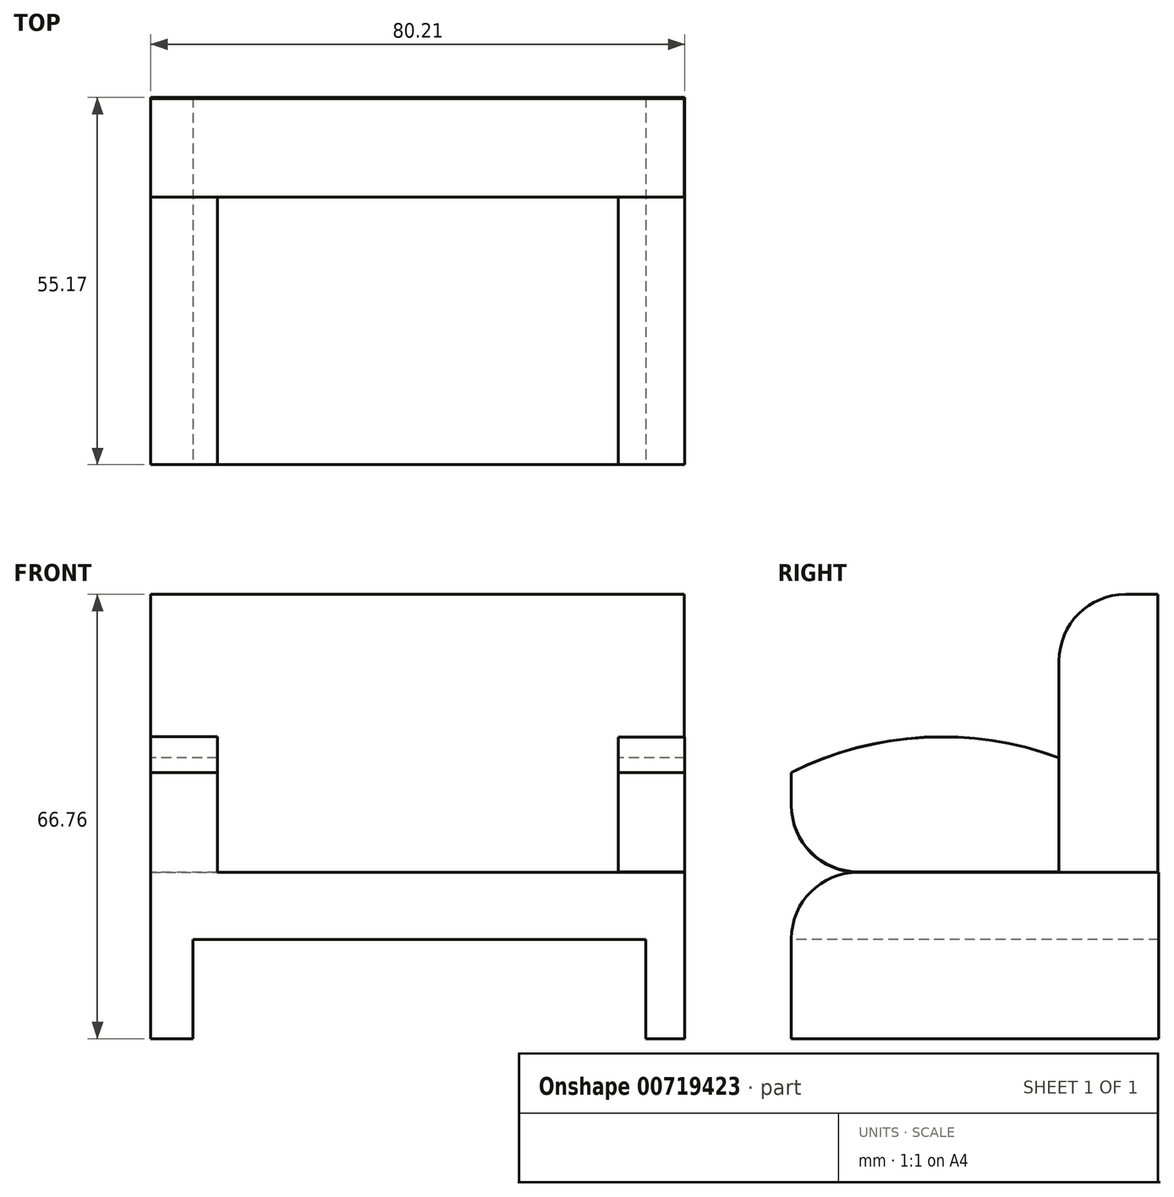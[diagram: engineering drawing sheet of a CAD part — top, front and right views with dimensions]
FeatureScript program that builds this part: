
annotation { "Feature Type Name" : "Feature", "Feature Type Description" : "" }
export const myFeature = defineFeature(function(context is Context, id is Id, definition is map)
    precondition{}
    {
        {
            var Q0;
            Q0=qCreatedBy(makeId("Top.planeOp"),FACE);
            var sketch = newSketch(context, id + "F0", { "sketchPlane" : qUnion([Q0])});
            skLineSegment(sketch, "E0.bottom", {"start": v(0, 0) * mm, "end": v(80.21, 0) * mm});
            skLineSegment(sketch, "E0.top", {"start": v(0, 55.17) * mm, "end": v(80.21, 55.17) * mm});
            skLineSegment(sketch, "E0.left", {"start": v(0, 0) * mm, "end": v(0, 55.17) * mm});
            skLineSegment(sketch, "E0.right", {"start": v(80.21, 0) * mm, "end": v(80.21, 55.17) * mm});
            skSolve(sketch);
        }
        {
            var Q0;
            Q0=makeQuery(id+"F0.imprint","IMPRINT",FACE,{"disambiguationData":[TD([[makeQuery(id+"F0.imprint","IMPRINT",EDGE,{"derivedFrom":sQuery(id+"F0.wireOp",EDGE,"E0.bottom")}),1.0]])]});
            extrude(context, id + "F1", {"entities" : qUnion([Q0]), "depth" : 25 * mm, "offsetDistance" : 25 * mm});
        }
        {
            var Q0;
            Q0=qCreatedBy(makeId("Front.planeOp"),FACE);
            cPlane(context, id + "F2", {"entities" : qUnion([Q0]), "cplaneType" : CPlaneType.OFFSET, "offset" : 55 * mm, "oppositeDirection" : true, "width" : 150 * mm, "height" : 150 * mm});
        }
        {
            var Q0;
            Q0=qCreatedBy(id+"F2.planeOp",FACE);
            var sketch = newSketch(context, id + "F3", { "sketchPlane" : qUnion([Q0])});
            skLineSegment(sketch, "E1.bottom", {"start": v(80.1, 0) * mm, "end": v(0, 0) * mm});
            skLineSegment(sketch, "E1.top", {"start": v(80.1, 66.76) * mm, "end": v(0, 66.76) * mm});
            skLineSegment(sketch, "E1.left", {"start": v(80.1, 0) * mm, "end": v(80.1, 66.76) * mm});
            skLineSegment(sketch, "E1.right", {"start": v(0, 0) * mm, "end": v(0, 66.76) * mm});
            skSolve(sketch);
        }
        {
            var Q0;
            Q0=qSketchRegion(id+"F3",true);
            extrude(context, id + "F4", {"entities" : qUnion([Q0]), "operationType" : NewBodyOperationType.ADD, "depth" : 14.8 * mm, "offsetDistance" : 25 * mm});
        }
        {
            var Q0;
            Q0=qCreatedBy(makeId("Right.planeOp"),FACE);
            var sketch = newSketch(context, id + "F5", { "sketchPlane" : qUnion([Q0])});
            skArc(sketch, "E2", {"start": v(40.2, 42.2) * mm, "mid": v(19.87, 45.28) * mm, "end": v(0, 40) * mm});
            skLineSegment(sketch, "E3", {"start": v(40.2, 42.2) * mm, "end": v(40.2, 25) * mm});
            skLineSegment(sketch, "E4", {"start": v(40.2, 25) * mm, "end": v(0, 25) * mm});
            skLineSegment(sketch, "E5", {"start": v(0, 25) * mm, "end": v(0, 40) * mm});
            skSolve(sketch);
        }
        {
            var Q0;
            Q0=qSketchRegion(id+"F5",true);
            extrude(context, id + "F6", {"entities" : qUnion([Q0]), "depth" : 10 * mm, "offsetDistance" : 25 * mm});
        }
        {
            var Q0;
            Q0=qCreatedBy(makeId("Right.planeOp"),FACE);
            cPlane(context, id + "F7", {"entities" : qUnion([Q0]), "cplaneType" : CPlaneType.OFFSET, "offset" : 70.21 * mm, "width" : 150 * mm, "height" : 150 * mm});
        }
        {
            var Q0;
            Q0=qCreatedBy(id+"F7.planeOp",FACE);
            var sketch = newSketch(context, id + "F8", { "sketchPlane" : qUnion([Q0])});
            skArc(sketch, "E6", {"start": v(40.2, 42.2) * mm, "mid": v(19.87, 45.27) * mm, "end": v(0, 40) * mm});
            skLineSegment(sketch, "E7", {"start": v(0, 40) * mm, "end": v(0, 25.08) * mm});
            skLineSegment(sketch, "E8", {"start": v(0, 25.08) * mm, "end": v(40.2, 25.08) * mm});
            skLineSegment(sketch, "E9", {"start": v(40.2, 25.08) * mm, "end": v(40.2, 42.2) * mm});
            skSolve(sketch);
        }
        {
            var Q0;
            Q0=qSketchRegion(id+"F8",true);
            extrude(context, id + "F9", {"entities" : qUnion([Q0]), "depth" : 10 * mm, "offsetDistance" : 25 * mm});
        }
        {
            var Q0;
            Q0=qCreatedBy(makeId("Front.planeOp"),FACE);
            var sketch = newSketch(context, id + "F10", { "sketchPlane" : qUnion([Q0])});
            skLineSegment(sketch, "E10.bottom", {"start": v(6.36, 0) * mm, "end": v(74.33, 0) * mm});
            skLineSegment(sketch, "E10.top", {"start": v(6.36, 14.87) * mm, "end": v(74.33, 14.87) * mm});
            skLineSegment(sketch, "E10.left", {"start": v(6.36, 0) * mm, "end": v(6.36, 14.87) * mm});
            skLineSegment(sketch, "E10.right", {"start": v(74.33, 0) * mm, "end": v(74.33, 14.87) * mm});
            skSolve(sketch);
        }
        {
            var Q0;
            Q0=qSketchRegion(id+"F10",true);
            extrude(context, id + "F11", {"entities" : qUnion([Q0]), "operationType" : NewBodyOperationType.REMOVE, "oppositeDirection" : true, "depth" : 99 * mm, "offsetDistance" : 25 * mm});
        }
        {
            var Q0;
            Q0=makeQuery(id+"F1.opExtrude","CAP_EDGE",EDGE,{"disambiguationData":[OSD([sQuery(id+"F0.wireOp",EDGE,"E0.bottom")])],"isStart":false});
            var Q1;
            Q1=makeQuery(id+"F6.opExtrude","SWEPT_EDGE",EDGE,{"disambiguationData":[OSD([sQuery(id+"F5.wireOp",EDGE,"E4"),sQuery(id+"F5.wireOp",EDGE,"E5")])]});
            var Q2;
            Q2=makeQuery(id+"F9.opExtrude","SWEPT_EDGE",EDGE,{"disambiguationData":[OSD([sQuery(id+"F8.wireOp",EDGE,"E7"),sQuery(id+"F8.wireOp",EDGE,"E8")])]});
            var Q3;
            Q3=makeQuery(id+"F4.opExtrude","CAP_EDGE",EDGE,{"disambiguationData":[OSD([sQuery(id+"F3.wireOp",EDGE,"E1.top")])],"isStart":false});
            fillet(context, id + "F12", {"entities" : qUnion([Q0, Q1, Q2, Q3]), "radius" : 10 * mm, "tangentPropagation" : true, "allowEdgeOverflow" : false});
        }
    });
